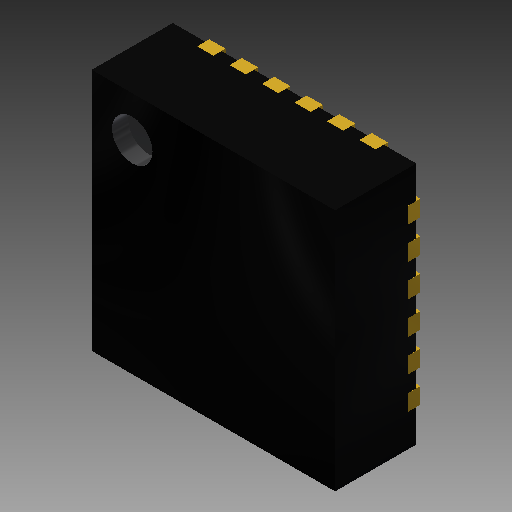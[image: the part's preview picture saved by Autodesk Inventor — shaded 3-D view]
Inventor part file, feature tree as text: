
AUTODESK INVENTOR PART (.ipt)
format: ipt  version: 2018 (Build 220112000, 112)  size: 381,952 bytes
history: native  units: mm
features: extrude x7, sketch x7, other x1
ambient origin geometry x8: Origin, YZ Plane, XZ Plane, XY Plane, X Axis, Y Axis, Z Axis, Center Point
bodies: Body1 (feature_tree)
feature tree (15):
  other  "Твердое тело1"
  extrude  "Выдавливание1"  Depth=3.0mm
  extrude  "Выдавливание2"  Depth=1.0mm TaperAngle=0.0deg
  extrude  "Выдавливание3"  Depth=0.5mm
  extrude  "Выдавливание4"  Depth=0.5mm
  extrude  "Выдавливание5"  Depth=0.5mm
  extrude  "Выдавливание6"  Depth=0.2mm TaperAngle=0.0deg
  extrude  "Выдавливание7"  Depth=0.3mm
  sketch  "Эскиз1"
  sketch  "Эскиз2"
  sketch  "Эскиз3"
  sketch  "Эскиз4"
  sketch  "Эскиз5"
  sketch  "Эскиз6"
  sketch  "Эскиз7"
